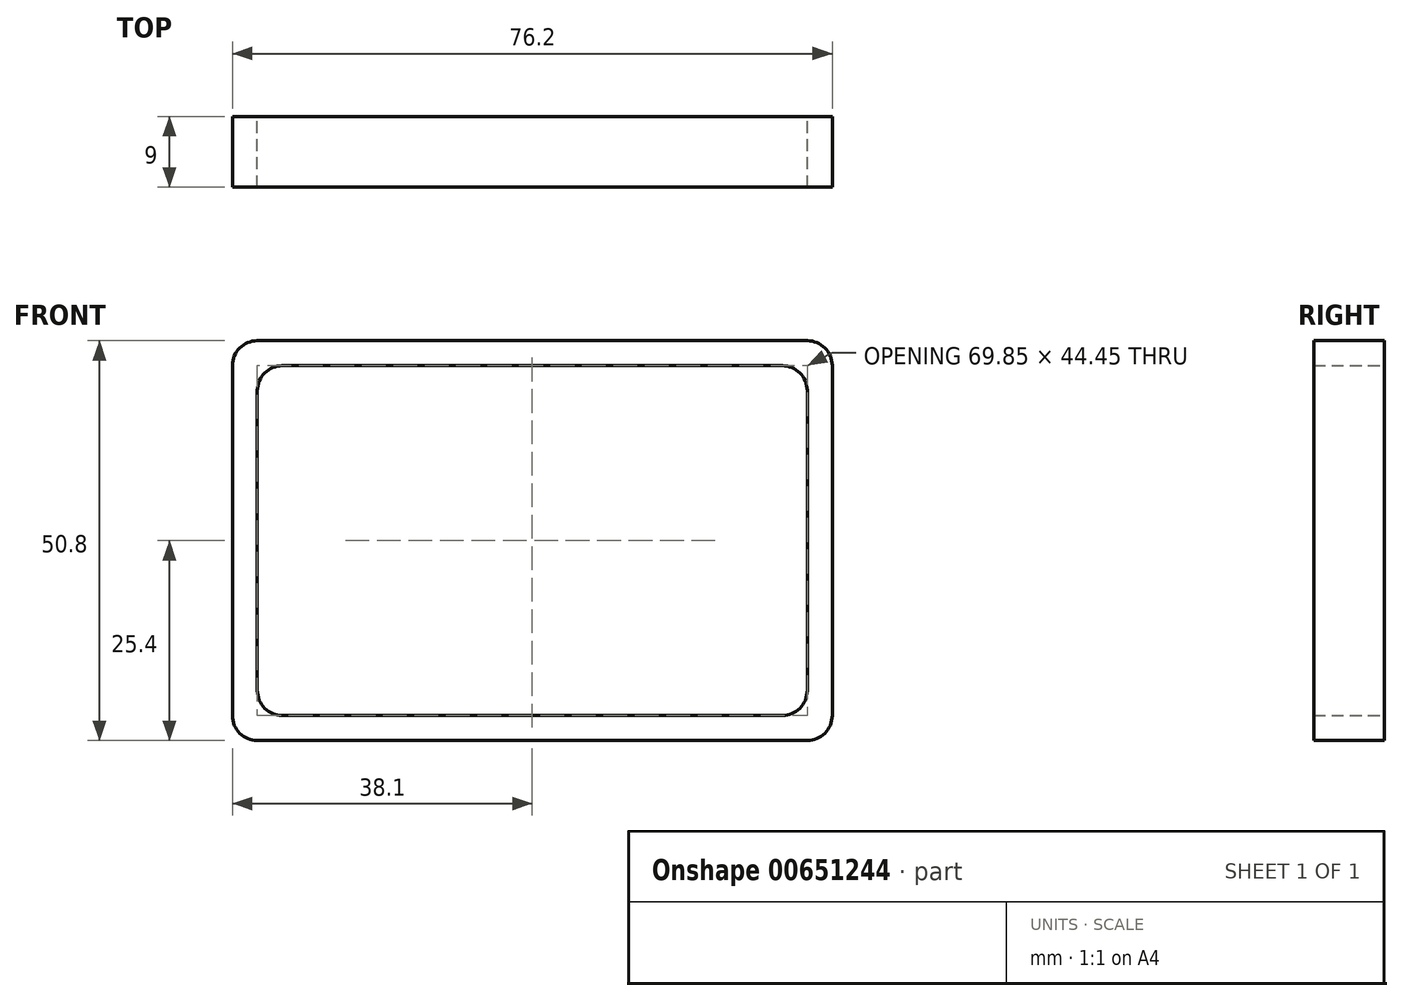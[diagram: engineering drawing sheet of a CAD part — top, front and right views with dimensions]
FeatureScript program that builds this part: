
annotation { "Feature Type Name" : "Feature", "Feature Type Description" : "" }
export const myFeature = defineFeature(function(context is Context, id is Id, definition is map)
    precondition{}
    {
        {
            var Q0;
            Q0=qCreatedBy(makeId("Front.planeOp"),FACE);
            var sketch = newSketch(context, id + "F0", { "sketchPlane" : qUnion([Q0])});
            skLineSegment(sketch, "E0.bottom", {"start": v(-38.1, -25.4) * mm, "end": v(38.1, -25.4) * mm});
            skLineSegment(sketch, "E0.top", {"start": v(-38.1, 25.4) * mm, "end": v(38.1, 25.4) * mm});
            skLineSegment(sketch, "E0.left", {"start": v(-38.1, -25.4) * mm, "end": v(-38.1, 25.4) * mm});
            skLineSegment(sketch, "E0.right", {"start": v(38.1, -25.4) * mm, "end": v(38.1, 25.4) * mm});
            skPoint(sketch, "E0.middle", {"position": v(0, 0) * mm});
            skLineSegment(sketch, "E1.bottom", {"start": v(34.93, -22.22) * mm, "end": v(-34.93, -22.23) * mm});
            skLineSegment(sketch, "E1.top", {"start": v(34.93, 22.23) * mm, "end": v(-34.93, 22.22) * mm});
            skLineSegment(sketch, "E1.left", {"start": v(34.93, -22.22) * mm, "end": v(34.93, 22.23) * mm});
            skLineSegment(sketch, "E1.right", {"start": v(-34.93, -22.23) * mm, "end": v(-34.93, 22.22) * mm});
            skSolve(sketch);
        }
        {
            assignVariable(context, id + "F1", {"name" : "Length", "anyValue" : 9});
        }
        {
            var Q0;
            Q0=makeQuery(id+"F0.imprint","IMPRINT",FACE,{"disambiguationData":[TD([[makeQuery(id+"F0.imprint","IMPRINT",EDGE,{"derivedFrom":sQuery(id+"F0.wireOp",EDGE,"E0.bottom")}),1.0]])]});
            extrude(context, id + "F2", {"entities" : qUnion([Q0]), "depth" : (getVariable(context, 'Length')) * mm, "offsetDistance" : 25.4 * mm});
        }
        {
            var Q0;
            Q0=makeQuery(id+"F2.opExtrude","SWEPT_EDGE",EDGE,{"disambiguationData":[OSD([sQuery(id+"F0.wireOp",EDGE,"E0.top"),sQuery(id+"F0.wireOp",EDGE,"E0.left")])]});
            var Q1;
            Q1=makeQuery(id+"F2.opExtrude","SWEPT_EDGE",EDGE,{"disambiguationData":[OSD([sQuery(id+"F0.wireOp",EDGE,"E0.top"),sQuery(id+"F0.wireOp",EDGE,"E0.right")])]});
            var Q2;
            Q2=makeQuery(id+"F2.opExtrude","SWEPT_EDGE",EDGE,{"disambiguationData":[OSD([sQuery(id+"F0.wireOp",EDGE,"E0.bottom"),sQuery(id+"F0.wireOp",EDGE,"E0.right")])]});
            var Q3;
            Q3=makeQuery(id+"F2.opExtrude","SWEPT_EDGE",EDGE,{"disambiguationData":[OSD([sQuery(id+"F0.wireOp",EDGE,"E0.bottom"),sQuery(id+"F0.wireOp",EDGE,"E0.left")])]});
            var Q4;
            Q4=makeQuery(id+"F2.opExtrude","SWEPT_EDGE",EDGE,{"disambiguationData":[OSD([sQuery(id+"F0.wireOp",EDGE,"E1.bottom"),sQuery(id+"F0.wireOp",EDGE,"E1.right")])]});
            var Q5;
            Q5=makeQuery(id+"F2.opExtrude","SWEPT_EDGE",EDGE,{"disambiguationData":[OSD([sQuery(id+"F0.wireOp",EDGE,"E1.top"),sQuery(id+"F0.wireOp",EDGE,"E1.right")])]});
            var Q6;
            Q6=makeQuery(id+"F2.opExtrude","SWEPT_EDGE",EDGE,{"disambiguationData":[OSD([sQuery(id+"F0.wireOp",EDGE,"E1.top"),sQuery(id+"F0.wireOp",EDGE,"E1.left")])]});
            var Q7;
            Q7=makeQuery(id+"F2.opExtrude","SWEPT_EDGE",EDGE,{"disambiguationData":[OSD([sQuery(id+"F0.wireOp",EDGE,"E1.bottom"),sQuery(id+"F0.wireOp",EDGE,"E1.left")])]});
            fillet(context, id + "F3", {"entities" : qUnion([Q0, Q1, Q2, Q3, Q4, Q5, Q6, Q7]), "radius" : 3.17 * mm, "tangentPropagation" : true, "allowEdgeOverflow" : false});
        }
    });
